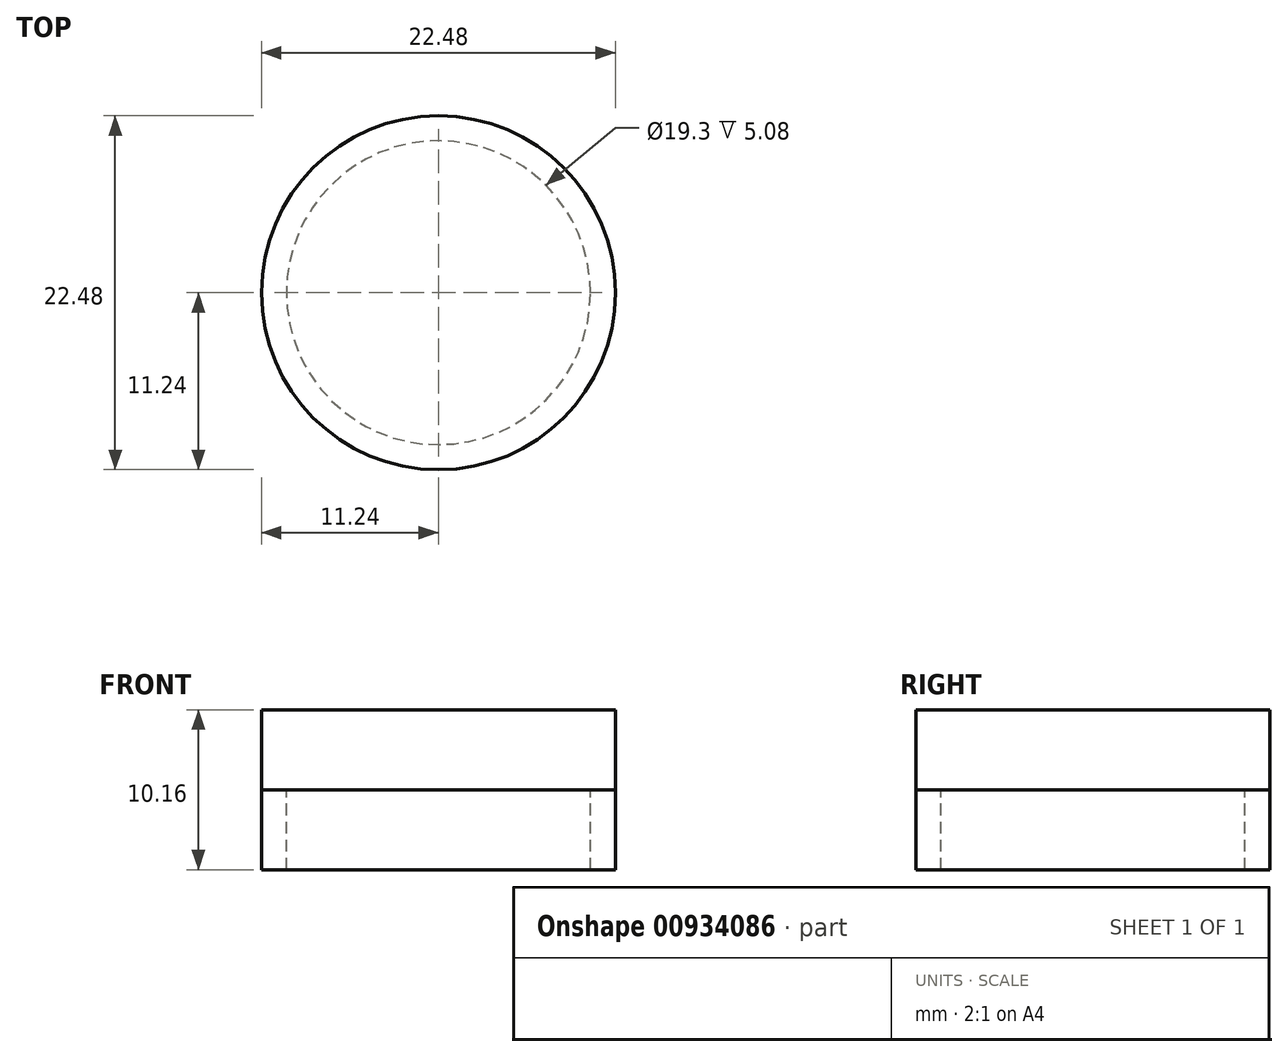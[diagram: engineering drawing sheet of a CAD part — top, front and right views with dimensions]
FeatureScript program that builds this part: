
annotation { "Feature Type Name" : "Feature", "Feature Type Description" : "" }
export const myFeature = defineFeature(function(context is Context, id is Id, definition is map)
    precondition{}
    {
        {
            var Q0;
            Q0=qCreatedBy(makeId("Top.planeOp"),FACE);
            var sketch = newSketch(context, id + "F0", { "sketchPlane" : qUnion([Q0])});
            skCircle(sketch, "E0", {"center": v(0, 0) * mm, "radius": 9.65 * mm});
            skCircle(sketch, "E1", {"center": v(0, 0) * mm, "radius": 11.24 * mm});
            skSolve(sketch);
        }
        {
            var Q0;
            Q0=makeQuery(id+"F0.imprint","IMPRINT",FACE,{"disambiguationData":[TD([[makeQuery(id+"F0.imprint","IMPRINT",EDGE,{"derivedFrom":sQuery(id+"F0.wireOp",EDGE,"E0")}),-1.0]])]});
            extrude(context, id + "F1", {"entities" : qUnion([Q0]), "oppositeDirection" : true, "depth" : 5.08 * mm, "offsetDistance" : 25.4 * mm});
        }
        {
            var Q0;
            Q0=makeQuery(id+"F0.imprint","IMPRINT",FACE,{"disambiguationData":[TD([[makeQuery(id+"F0.imprint","IMPRINT",EDGE,{"derivedFrom":sQuery(id+"F0.wireOp",EDGE,"E0")}),1.0]])]});
            var Q1;
            Q1=makeQuery(id+"F0.imprint","IMPRINT",FACE,{"disambiguationData":[TD([[makeQuery(id+"F0.imprint","IMPRINT",EDGE,{"derivedFrom":sQuery(id+"F0.wireOp",EDGE,"E0")}),-1.0]])]});
            extrude(context, id + "F2", {"entities" : qUnion([Q0, Q1]), "depth" : 5.08 * mm, "offsetDistance" : 25.4 * mm});
        }
    });
